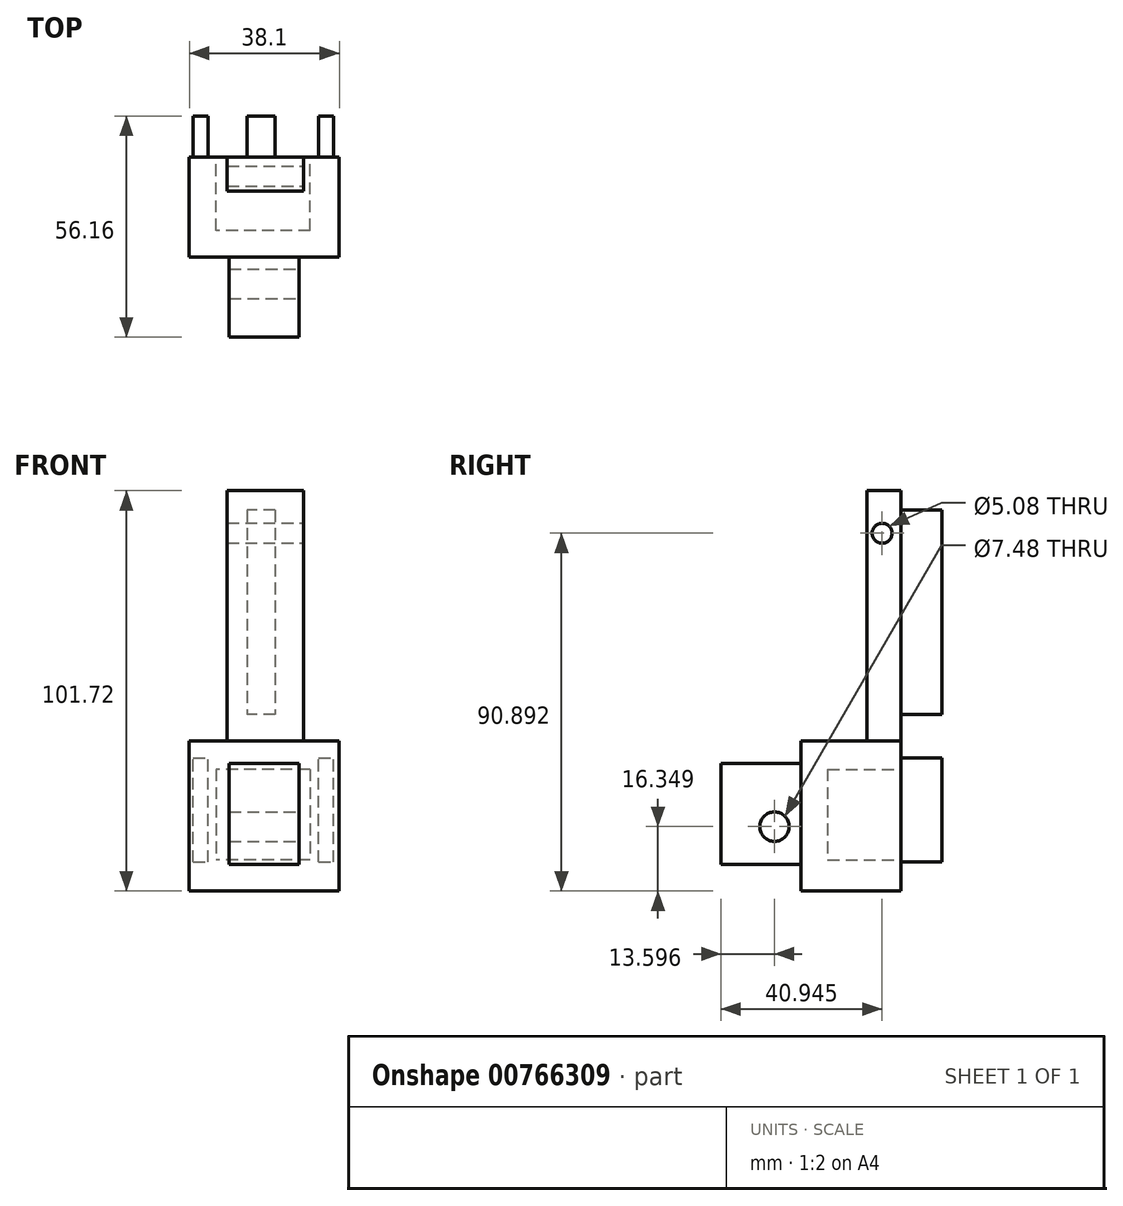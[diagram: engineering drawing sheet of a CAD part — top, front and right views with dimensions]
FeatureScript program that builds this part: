
annotation { "Feature Type Name" : "Feature", "Feature Type Description" : "" }
export const myFeature = defineFeature(function(context is Context, id is Id, definition is map)
    precondition{}
    {
        {
            var Q0;
            Q0=qCreatedBy(makeId("Front.planeOp"),FACE);
            var sketch = newSketch(context, id + "F0", { "sketchPlane" : qUnion([Q0])});
            skLineSegment(sketch, "E0.bottom", {"start": v(4.3, -38.03) * mm, "end": v(42.4, -38.03) * mm});
            skLineSegment(sketch, "E0.top", {"start": v(4.3, -76.13) * mm, "end": v(42.4, -76.13) * mm});
            skLineSegment(sketch, "E0.left", {"start": v(4.3, -38.03) * mm, "end": v(4.3, -76.13) * mm});
            skLineSegment(sketch, "E0.right", {"start": v(42.4, -38.03) * mm, "end": v(42.4, -76.13) * mm});
            skCircle(sketch, "E1", {"center": v(29.7, -57.08) * mm, "radius": 12.7 * mm});
            skSolve(sketch);
        }
        {
            var Q0;
            Q0 = qSketchRegion(id + "F0", true);
            extrude(context, id + "F1", {"entities" : qUnion([Q0]), "oppositeDirection" : true, "depth" : 25.4 * mm, "offsetDistance" : 25.4 * mm});
        }
        {
            var Q0;
            Q0=makeQuery(id+"F1.opExtrude","SWEPT_FACE",FACE,{"disambiguationData":[OSD([sQuery(id+"F0.wireOp",EDGE,"E0.bottom")])]});
            var sketch = newSketch(context, id + "F2", { "sketchPlane" : qUnion([Q0])});
            skLineSegment(sketch, "E2.bottom", {"start": v(13.95, 25.4) * mm, "end": v(33.37, 25.4) * mm});
            skLineSegment(sketch, "E2.top", {"start": v(13.95, 16.81) * mm, "end": v(33.37, 16.81) * mm});
            skLineSegment(sketch, "E2.left", {"start": v(13.95, 25.4) * mm, "end": v(13.95, 16.81) * mm});
            skLineSegment(sketch, "E2.right", {"start": v(33.37, 25.4) * mm, "end": v(33.37, 16.81) * mm});
            skSolve(sketch);
        }
        {
            var Q0;
            Q0 = qSketchRegion(id + "F2", true);
            extrude(context, id + "F3", {"entities" : qUnion([Q0]), "operationType" : NewBodyOperationType.ADD, "depth" : 63.62 * mm, "offsetDistance" : 25.4 * mm});
        }
        {
            var Q0;
            Q0=makeQuery(id+"F3.boolean.opBoolean","MERGE",FACE,{"derivedFrom":[makeQuery(id+"F1.opExtrude","CAP_FACE",FACE,{"disambiguationData":[OSD([sQuery(id+"F0.wireOp",EDGE,"E0.bottom"),sQuery(id+"F0.wireOp",EDGE,"E0.top"),sQuery(id+"F0.wireOp",EDGE,"E0.left"),sQuery(id+"F0.wireOp",EDGE,"E0.right")])],"isStart":false}),makeQuery(id+"F3.opExtrude","SWEPT_FACE",FACE,{"disambiguationData":[OSD([sQuery(id+"F2.wireOp",EDGE,"E2.bottom")])]})]});
            var sketch = newSketch(context, id + "F4", { "sketchPlane" : qUnion([Q0])});
            skLineSegment(sketch, "E3.bottom", {"start": v(-35.05, -45.19) * mm, "end": v(-11.06, -45.19) * mm});
            skLineSegment(sketch, "E3.top", {"start": v(-35.05, -68.3) * mm, "end": v(-11.06, -68.3) * mm});
            skLineSegment(sketch, "E3.left", {"start": v(-35.05, -45.19) * mm, "end": v(-35.05, -68.3) * mm});
            skLineSegment(sketch, "E3.right", {"start": v(-11.06, -45.19) * mm, "end": v(-11.06, -68.3) * mm});
            skSolve(sketch);
        }
        {
            var Q0;
            Q0=makeQuery(id+"F4.imprint","IMPRINT",FACE,{"disambiguationData":[TD([[makeQuery(id+"F4.imprint","IMPRINT",EDGE,{"derivedFrom":sQuery(id+"F4.wireOp",EDGE,"E3.bottom")}),-1.0]])]});
            var Q1;
            Q1=makeQuery(id+"F1.opExtrude","CAP_FACE",FACE,{"disambiguationData":[OSD([sQuery(id+"F0.wireOp",EDGE,"E0.bottom"),sQuery(id+"F0.wireOp",EDGE,"E0.top"),sQuery(id+"F0.wireOp",EDGE,"E0.left"),sQuery(id+"F0.wireOp",EDGE,"E0.right")])],"isStart":true});
            extrude(context, id + "F5", {"entities" : qUnion([Q0, Q1]), "operationType" : NewBodyOperationType.REMOVE, "oppositeDirection" : true, "depth" : 18.6 * mm, "offsetDistance" : 25.4 * mm});
        }
        {
            var Q0;
            Q0=makeQuery(id+"F3.opExtrude","SWEPT_FACE",FACE,{"disambiguationData":[OSD([sQuery(id+"F2.wireOp",EDGE,"E2.right")])]});
            var sketch = newSketch(context, id + "F6", { "sketchPlane" : qUnion([Q0])});
            skCircle(sketch, "E4", {"center": v(20.62, 14.76) * mm, "radius": 2.54 * mm});
            skSolve(sketch);
        }
        {
            var Q0;
            Q0=makeQuery(id+"F6.imprint","IMPRINT",FACE,{"disambiguationData":[TD([[makeQuery(id+"F6.imprint","IMPRINT",EDGE,{"derivedFrom":sQuery(id+"F6.wireOp",EDGE,"E4")}),1.0]])]});
            var Q1;
            Q1=sQuery(id+"F6.wireOp",EDGE,"E4");
            extrude(context, id + "F7", {"entities" : qUnion([Q0]), "operationType" : NewBodyOperationType.REMOVE, "surfaceEntities" : qUnion([Q1]), "oppositeDirection" : true, "depth" : 25.4 * mm, "offsetDistance" : 25.4 * mm});
        }
        {
            var Q0;
            Q0=makeQuery(id+"F3.boolean.opBoolean","MERGE",FACE,{"derivedFrom":[makeQuery(id+"F1.opExtrude","CAP_FACE",FACE,{"disambiguationData":[OSD([sQuery(id+"F0.wireOp",EDGE,"E0.bottom"),sQuery(id+"F0.wireOp",EDGE,"E0.top"),sQuery(id+"F0.wireOp",EDGE,"E0.left"),sQuery(id+"F0.wireOp",EDGE,"E0.right")])],"isStart":false}),makeQuery(id+"F3.opExtrude","SWEPT_FACE",FACE,{"disambiguationData":[OSD([sQuery(id+"F2.wireOp",EDGE,"E2.bottom")])]})]});
            var sketch = newSketch(context, id + "F8", { "sketchPlane" : qUnion([Q0])});
            skLineSegment(sketch, "E5.bottom", {"start": v(-5.32, -68.76) * mm, "end": v(-9.13, -68.76) * mm});
            skLineSegment(sketch, "E5.top", {"start": v(-5.32, -42.35) * mm, "end": v(-9.13, -42.35) * mm});
            skLineSegment(sketch, "E5.left", {"start": v(-5.32, -68.76) * mm, "end": v(-5.32, -42.35) * mm});
            skLineSegment(sketch, "E5.right", {"start": v(-9.13, -68.76) * mm, "end": v(-9.13, -42.35) * mm});
            skLineSegment(sketch, "E6.bottom", {"start": v(-37.15, -68.76) * mm, "end": v(-40.96, -68.76) * mm});
            skLineSegment(sketch, "E6.top", {"start": v(-37.15, -42.35) * mm, "end": v(-40.96, -42.35) * mm});
            skLineSegment(sketch, "E6.left", {"start": v(-37.15, -68.76) * mm, "end": v(-37.15, -42.35) * mm});
            skLineSegment(sketch, "E6.right", {"start": v(-40.96, -68.76) * mm, "end": v(-40.96, -42.35) * mm});
            skSolve(sketch);
        }
        {
            var Q0;
            Q0 = qSketchRegion(id + "F8", true);
            extrude(context, id + "F9", {"entities" : qUnion([Q0]), "operationType" : NewBodyOperationType.ADD, "depth" : 10.44 * mm, "offsetDistance" : 25.4 * mm});
        }
        {
            var Q0;
            Q0=makeQuery(id+"F1.opExtrude","CAP_FACE",FACE,{"disambiguationData":[OSD([sQuery(id+"F0.wireOp",EDGE,"E0.bottom"),sQuery(id+"F0.wireOp",EDGE,"E0.top"),sQuery(id+"F0.wireOp",EDGE,"E0.left"),sQuery(id+"F0.wireOp",EDGE,"E0.right")])],"isStart":true});
            var sketch = newSketch(context, id + "F10", { "sketchPlane" : qUnion([Q0])});
            skLineSegment(sketch, "E7.bottom", {"start": v(32.25, -69.43) * mm, "end": v(14.47, -69.43) * mm});
            skLineSegment(sketch, "E7.top", {"start": v(32.25, -43.77) * mm, "end": v(14.47, -43.77) * mm});
            skLineSegment(sketch, "E7.left", {"start": v(32.25, -69.43) * mm, "end": v(32.25, -43.77) * mm});
            skLineSegment(sketch, "E7.right", {"start": v(14.47, -69.43) * mm, "end": v(14.47, -43.77) * mm});
            skSolve(sketch);
        }
        {
            var Q0;
            Q0 = qSketchRegion(id + "F10", true);
            extrude(context, id + "F11", {"entities" : qUnion([Q0]), "operationType" : NewBodyOperationType.ADD, "depth" : 20.32 * mm, "offsetDistance" : 25.4 * mm});
        }
        {
            var Q0;
            Q0=makeQuery(id+"F11.opExtrude","SWEPT_FACE",FACE,{"disambiguationData":[OSD([sQuery(id+"F10.wireOp",EDGE,"E7.left")])]});
            var sketch = newSketch(context, id + "F12", { "sketchPlane" : qUnion([Q0])});
            skCircle(sketch, "E8", {"center": v(-6.72, -59.78) * mm, "radius": 3.74 * mm});
            skSolve(sketch);
        }
        {
            var Q0;
            Q0 = qSketchRegion(id + "F12", true);
            extrude(context, id + "F13", {"entities" : qUnion([Q0]), "operationType" : NewBodyOperationType.REMOVE, "oppositeDirection" : true, "depth" : 25.4 * mm, "offsetDistance" : 25.4 * mm});
        }
        {
            var Q0;
            Q0=makeQuery(id+"F3.boolean.opBoolean","MERGE",FACE,{"derivedFrom":[makeQuery(id+"F1.opExtrude","CAP_FACE",FACE,{"disambiguationData":[OSD([sQuery(id+"F0.wireOp",EDGE,"E0.bottom"),sQuery(id+"F0.wireOp",EDGE,"E0.top"),sQuery(id+"F0.wireOp",EDGE,"E0.left"),sQuery(id+"F0.wireOp",EDGE,"E0.right")])],"isStart":false}),makeQuery(id+"F3.opExtrude","SWEPT_FACE",FACE,{"disambiguationData":[OSD([sQuery(id+"F2.wireOp",EDGE,"E2.bottom")])]})]});
            var sketch = newSketch(context, id + "F14", { "sketchPlane" : qUnion([Q0])});
            skLineSegment(sketch, "E9.bottom", {"start": v(-26.14, 20.63) * mm, "end": v(-19.03, 20.63) * mm});
            skLineSegment(sketch, "E9.top", {"start": v(-26.14, -31.25) * mm, "end": v(-19.03, -31.25) * mm});
            skLineSegment(sketch, "E9.left", {"start": v(-26.14, 20.63) * mm, "end": v(-26.14, -31.25) * mm});
            skLineSegment(sketch, "E9.right", {"start": v(-19.03, 20.63) * mm, "end": v(-19.03, -31.25) * mm});
            skSolve(sketch);
        }
        {
            var Q0;
            Q0 = qSketchRegion(id + "F14", true);
            extrude(context, id + "F15", {"entities" : qUnion([Q0]), "operationType" : NewBodyOperationType.ADD, "depth" : 10.44 * mm, "offsetDistance" : 25.4 * mm});
        }
    });
